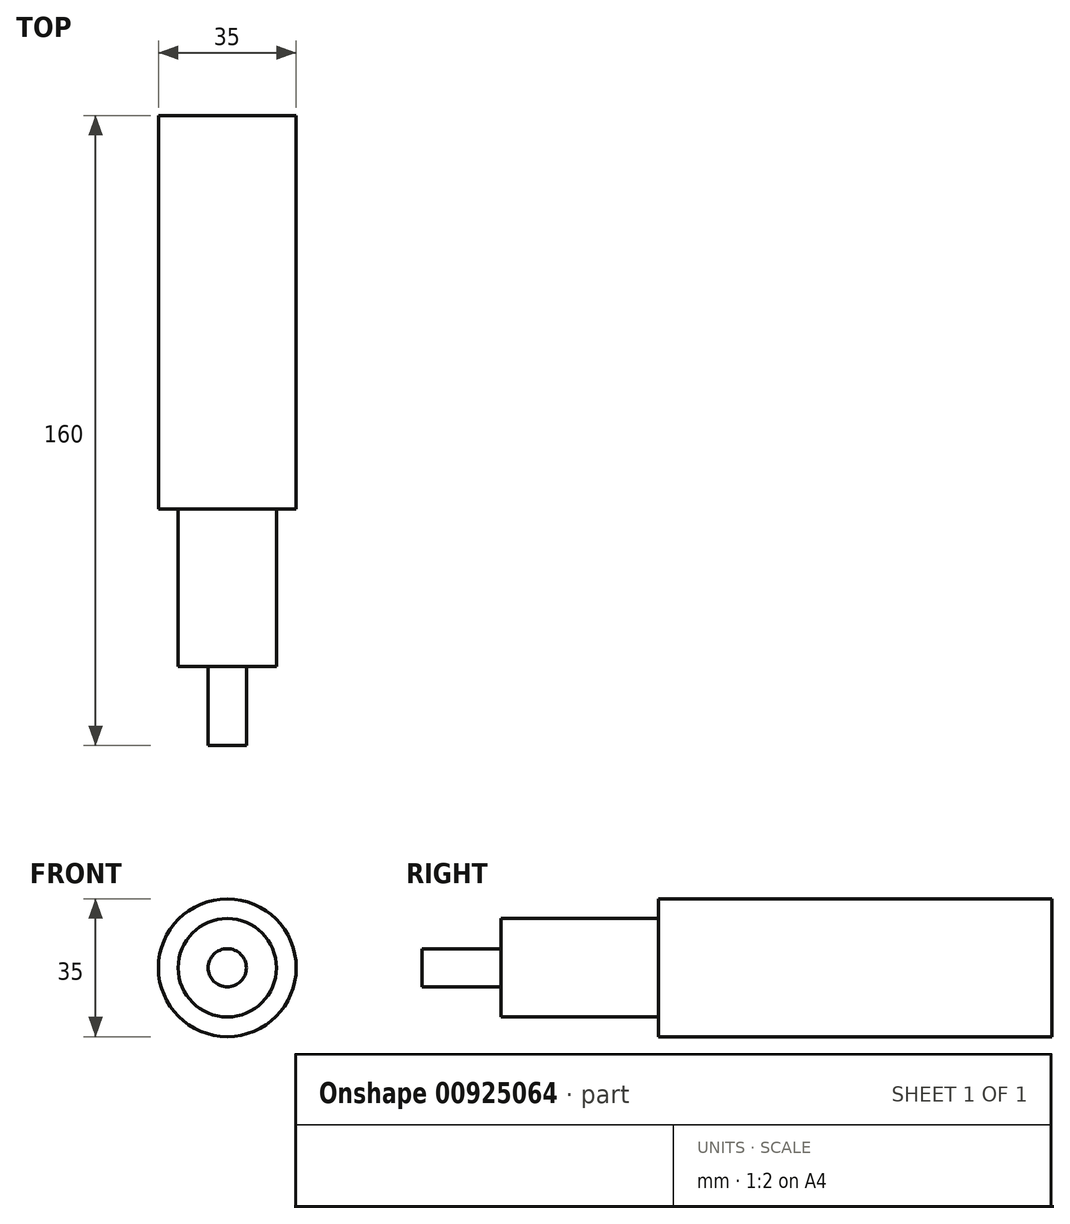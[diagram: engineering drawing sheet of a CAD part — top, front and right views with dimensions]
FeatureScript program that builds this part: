
annotation { "Feature Type Name" : "Feature", "Feature Type Description" : "" }
export const myFeature = defineFeature(function(context is Context, id is Id, definition is map)
    precondition{}
    {
        {
            var Q0;
            Q0=qCreatedBy(makeId("Front.planeOp"),FACE);
            var sketch = newSketch(context, id + "F0", { "sketchPlane" : qUnion([Q0])});
            skCircle(sketch, "E0", {"center": v(0, 0) * mm, "radius": 4.85 * mm});
            skSolve(sketch);
        }
        {
            var Q0;
            Q0 = qSketchRegion(id + "F0", true);
            extrude(context, id + "F1", {"entities" : qUnion([Q0]), "depth" : 20 * mm, "offsetDistance" : 25.4 * mm});
        }
        {
            var Q0;
            Q0=qCreatedBy(makeId("Front.planeOp"),FACE);
            var sketch = newSketch(context, id + "F2", { "sketchPlane" : qUnion([Q0])});
            skCircle(sketch, "E1", {"center": v(0, 0) * mm, "radius": 12.5 * mm});
            skSolve(sketch);
        }
        {
            var Q0;
            Q0 = qSketchRegion(id + "F2", true);
            extrude(context, id + "F3", {"entities" : qUnion([Q0]), "operationType" : NewBodyOperationType.ADD, "oppositeDirection" : true, "depth" : 40 * mm, "offsetDistance" : 25.4 * mm});
        }
        {
            var Q0;
            Q0=makeQuery(id+"F3.opExtrude","CAP_FACE",FACE,{"disambiguationData":[OSD([sQuery(id+"F2.wireOp",EDGE,"E1")])],"isStart":false});
            var sketch = newSketch(context, id + "F4", { "sketchPlane" : qUnion([Q0])});
            skCircle(sketch, "E2", {"center": v(0, 0) * mm, "radius": 17.5 * mm});
            skSolve(sketch);
        }
        {
            var Q0;
            Q0 = qSketchRegion(id + "F4", true);
            extrude(context, id + "F5", {"entities" : qUnion([Q0]), "operationType" : NewBodyOperationType.ADD, "depth" : 100 * mm, "offsetDistance" : 25.4 * mm});
        }
    });
